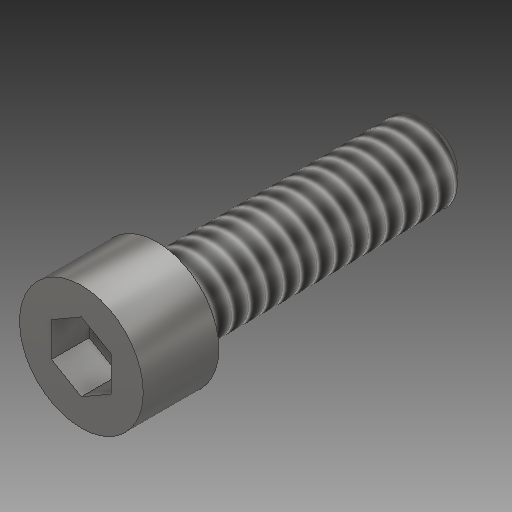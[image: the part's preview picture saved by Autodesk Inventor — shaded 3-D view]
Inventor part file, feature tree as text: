
AUTODESK INVENTOR PART (.ipt)
format: ipt  version: 2019 (Build 230136000, 136)  size: 162,816 bytes
history: native  units: in
note: dims shown in document units (in); Inventor stores cm internally (conversion verified against a paired STEP export)
features: other x3, sketch x3
ambient origin geometry x8: Origin, YZ Plane, XZ Plane, XY Plane, X Axis, Y Axis, Z Axis, Center Point
bodies: Solid1 (feature_tree)
feature tree (6):
  other  "6-32 SHCS x500.ipt"
  other  "Solid1::6-32 SHCS x500.ipt"
  other  "TaggingFeature1"
  sketch  "Sketch1"  dims[d0=0.3937in]
  sketch  "Sketch2"
  sketch  "Sketch3"
